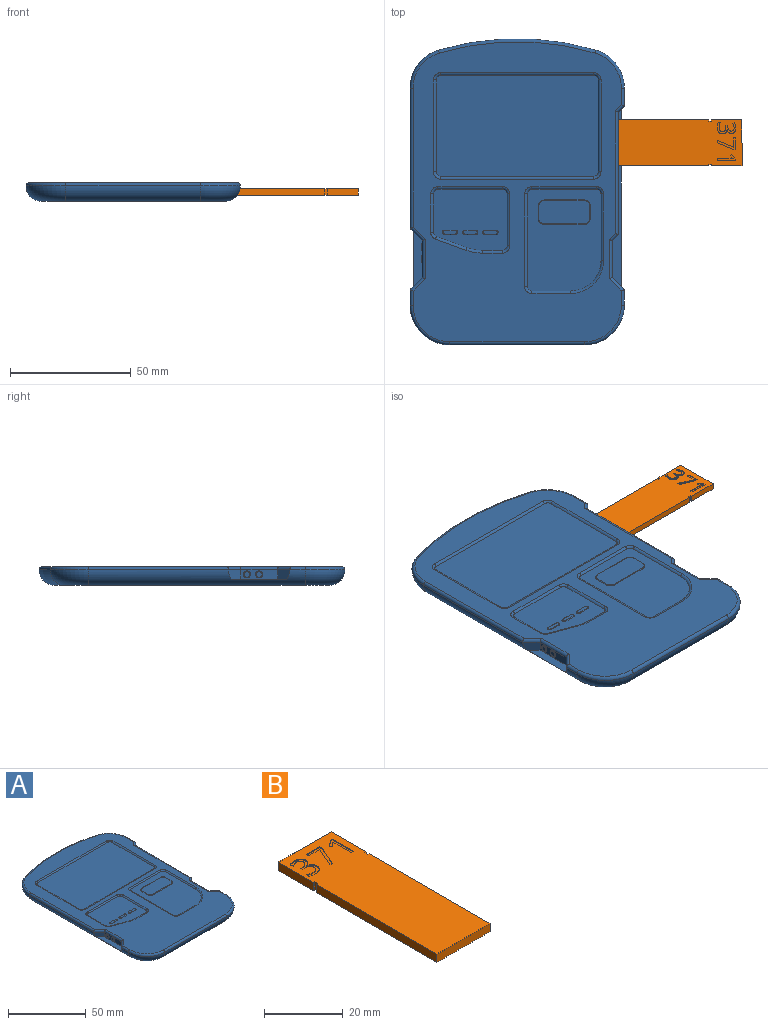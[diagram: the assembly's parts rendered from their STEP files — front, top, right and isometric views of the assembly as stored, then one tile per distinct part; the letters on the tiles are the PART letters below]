
ASSEMBLY  parts=2 mates=1
PART A: 139 faces, bbox 92.2x138.4x11.5 mm
  f0: plane 15.24x3.81mm, normal (1,0,0), area 17.9mm2, adj f1,f24,f25,f36,f129,f130,f131,f132
  f1: plane 73.66x3.81mm, normal (0,0,1), area 130mm2, adj f0,f2,f3,f23,f24,f25,f114,f116
  f2: cylinder r=6.35mm len=89.9mm, axis (0,1,0), area 580.4mm2, adj f1,f7,f11,f13,f23,f25,f31,f40
  f3: plane 50.8x3.81mm, normal (1,0,0), area 175.7mm2, adj f1,f23,f24,f32,f95,f96,f97,f98
  f4: plane 30.54x25.4mm, normal (0,0,1), area 685.8mm2, adj f49,f50,f51,f52,f53,f54,f55,f56
  f5: plane 124.46x86.36mm, normal (0,0,1), area 4712mm2, adj f15,f16,f17,f18,f19,f20,f21,f22
  f6: cylinder r=6.35mm len=89.9mm, axis (0,-1,0), area 798.1mm2, adj f7,f8,f10,f26,f27,f29,f39,f47
  f7: plane 114.3x76.2mm, normal (0,0,-1), area 8471mm2, adj f2,f6,f8,f9,f10,f11,f12,f13
  f8: torus R=10.16mm, axis (0,0,1), area 222.5mm2, adj f6,f7,f9,f46
  f9: cylinder r=6.35mm len=55.88mm, axis (1,0,0), area 557.4mm2, adj f7,f8,f11,f44
  f10: torus R=10.16mm, axis (0,0,1), area 181.5mm2, adj f6,f7,f12,f37
  f11: torus R=10.16mm, axis (0,0,1), area 222.5mm2, adj f2,f7,f9,f42
  f12: torus R=107.95mm, axis (0,0,1), area 647.3mm2, adj f7,f10,f13,f35
  f13: torus R=10.16mm, axis (0,0,1), area 181.5mm2, adj f2,f7,f12,f33
  f14: plane 67.31x41.91mm, normal (0,0,1), area 2817.8mm2, adj f15,f16,f17,f18,f19,f20,f21,f22
  f15: cylinder r=1.27mm len=63.5mm, axis (-1,0,0), area 84.5mm2, adj f5,f14,f16,f17
  f16: torus R=3mm, axis (0,0,1), area 5mm2, adj f5,f14,f15,f18
  f17: torus R=3mm, axis (0,0,1), area 5mm2, adj f5,f14,f15,f19
  f18: cylinder r=1.27mm len=38.1mm, axis (0,1,0), area 50.7mm2, adj f5,f14,f16,f20
  f19: cylinder r=1.27mm len=38.1mm, axis (0,1,0), area 50.7mm2, adj f5,f14,f17,f21
  f20: torus R=3mm, axis (0,0,1), area 5mm2, adj f5,f14,f18,f22
  f21: torus R=3mm, axis (0,0,1), area 5mm2, adj f5,f14,f19,f22
  f22: cylinder r=1.27mm len=63.5mm, axis (-1,0,0), area 84.5mm2, adj f5,f14,f20,f21
  f23: plane 3.81x2.54mm, normal (0.71,-0.71,0), area 11.5mm2, adj f1,f2,f3,f30
  f24: plane 3.81x2.54mm, normal (0.71,-0.71,0), area 13.7mm2, adj f0,f1,f3,f34
  f25: plane 5.08x5.08mm, normal (0.71,0.71,0), area 25.2mm2, adj f0,f1,f2,f38
  f26: plane 5.7x5.7mm, normal (-0.71,-0.71,0), area 25.2mm2, adj f6,f28,f29,f41
  f27: plane 5.7x5.7mm, normal (-0.71,0.71,0), area 25.2mm2, adj f6,f28,f29,f45
  f28: plane 15.24x3.81mm, normal (-1,0,0), area 44.7mm2, adj f26,f27,f29,f43,f122,f123
  f29: plane 22.86x3.81mm, normal (0,0,1), area 72.6mm2, adj f6,f26,f27,f28
  f30: cylinder r=1.27mm len=3.81mm, axis (0.71,0.71,0), area 7.2mm2, adj f5,f23,f31,f32
  f31: cylinder r=1.27mm len=7.35mm, axis (0,-1,0), area 14.1mm2, adj f2,f5,f30,f33
  f32: cylinder r=1.27mm len=51.33mm, axis (0,1,0), area 101.3mm2, adj f3,f5,f30,f34
  f33: torus R=15.24mm, axis (0,0,1), area 41mm2, adj f5,f13,f31,f35
  f34: cylinder r=1.27mm len=3.81mm, axis (0.71,0.71,0), area 7.2mm2, adj f5,f24,f32,f36
  f35: torus R=113.03mm, axis (0,0,1), area 131.6mm2, adj f5,f12,f33,f37
  f36: cylinder r=1.27mm len=16.29mm, axis (0,1,0), area 31.5mm2, adj f0,f5,f34,f38
  f37: torus R=15.24mm, axis (0,0,1), area 41mm2, adj f5,f10,f35,f39
  f38: cylinder r=1.27mm len=6.35mm, axis (-0.71,0.71,0), area 14.3mm2, adj f5,f25,f36,f40
  f39: cylinder r=1.27mm len=58.15mm, axis (0,1,0), area 115.5mm2, adj f5,f6,f37,f41
  f40: cylinder r=1.27mm len=6.35mm, axis (0,-1,0), area 12.1mm2, adj f2,f5,f38,f42
  f41: cylinder r=1.27mm len=6.35mm, axis (0.71,-0.71,0), area 14.3mm2, adj f5,f26,f39,f43
  f42: torus R=15.24mm, axis (0,0,1), area 50.3mm2, adj f5,f11,f40,f44
  f43: cylinder r=1.27mm len=16.29mm, axis (0,-1,0), area 31.5mm2, adj f5,f28,f41,f45
  f44: cylinder r=1.27mm len=55.88mm, axis (-1,0,0), area 111.5mm2, adj f5,f9,f42,f46
  f45: cylinder r=1.27mm len=6.35mm, axis (-0.71,-0.71,0), area 14.3mm2, adj f5,f27,f43,f47
  f46: torus R=15.24mm, axis (0,0,1), area 50.3mm2, adj f5,f8,f44,f47
  f47: cylinder r=1.27mm len=6.35mm, axis (0,1,0), area 12.1mm2, adj f5,f6,f45,f46
  f48: plane 42.2x30.54mm, normal (0,0,1), area 1037.6mm2, adj f59,f60,f61,f62,f63,f64,f65,f66
  f49: cylinder r=1.27mm len=8.26mm, axis (-1,0,0), area 11mm2, adj f4,f5,f50,f51
  f50: torus R=20.15mm, axis (0,0,1), area 9.1mm2, adj f4,f5,f49,f52
  f51: torus R=3mm, axis (0,0,1), area 5mm2, adj f4,f5,f49,f53
  f52: cylinder r=1.27mm len=12.99mm, axis (-0.94,0.34,0), area 17.9mm2, adj f4,f5,f50,f54
  f53: cylinder r=1.27mm len=21.59mm, axis (0,1,0), area 28.7mm2, adj f4,f5,f51,f55
  f54: torus R=3mm, axis (0,0,1), area 3.9mm2, adj f4,f5,f52,f56
  f55: torus R=3mm, axis (0,0,1), area 5mm2, adj f4,f5,f53,f57
  f56: cylinder r=1.27mm len=15.97mm, axis (0,1,0), area 21.2mm2, adj f4,f5,f54,f58
  f57: cylinder r=1.27mm len=26.73mm, axis (-1,0,0), area 35.6mm2, adj f4,f5,f55,f58
  f58: torus R=3mm, axis (0,0,1), area 5mm2, adj f4,f5,f56,f57
  f59: torus R=3mm, axis (0,0,1), area 5mm2, adj f5,f48,f60,f61
  f60: cylinder r=1.27mm len=27.6mm, axis (0,-1,0), area 36.7mm2, adj f5,f48,f59,f62
  f61: cylinder r=1.27mm len=26.73mm, axis (-1,0,0), area 35.6mm2, adj f5,f48,f59,f63
  f62: torus R=13.8mm, axis (0,0,1), area 27.6mm2, adj f5,f48,f60,f64
  f63: torus R=3mm, axis (0,0,1), area 5mm2, adj f5,f48,f61,f65
  f64: cylinder r=1.27mm len=15.94mm, axis (1,0,0), area 21.2mm2, adj f5,f48,f62,f66
  f65: cylinder r=1.27mm len=38.39mm, axis (0,1,0), area 51.1mm2, adj f5,f48,f63,f66
  f66: torus R=3mm, axis (0,0,1), area 5mm2, adj f5,f48,f64,f65
  f67: plane 5.84x1.4mm, normal (0,0,1), area 7.7mm2, adj f78,f79,f80,f81
  f68: plane 5.84x1.4mm, normal (0,0,1), area 7.7mm2, adj f74,f75,f76,f77
  f69: plane 5.84x1.4mm, normal (0,0,1), area 7.7mm2, adj f70,f71,f72,f73
  f70: cylinder r=0.25mm len=4.45mm, axis (-1,0,0), area 1.8mm2, adj f4,f69,f71,f72
  f71: torus R=0.7mm, axis (0,0,1), area 1.1mm2, adj f4,f69,f70,f73
  f72: torus R=0.7mm, axis (0,0,1), area 1.1mm2, adj f4,f69,f70,f73
  f73: cylinder r=0.25mm len=4.45mm, axis (1,0,0), area 1.8mm2, adj f4,f69,f71,f72
  f74: torus R=0.7mm, axis (0,0,1), area 1.1mm2, adj f4,f68,f75,f76
  f75: cylinder r=0.25mm len=4.45mm, axis (-1,0,0), area 1.8mm2, adj f4,f68,f74,f77
  f76: cylinder r=0.25mm len=4.45mm, axis (1,0,0), area 1.8mm2, adj f4,f68,f74,f77
  f77: torus R=0.7mm, axis (0,0,1), area 1.1mm2, adj f4,f68,f75,f76
  f78: cylinder r=0.25mm len=4.45mm, axis (1,0,0), area 1.8mm2, adj f4,f67,f79,f80
  f79: torus R=0.7mm, axis (0,0,1), area 1.1mm2, adj f4,f67,f78,f81
  f80: torus R=0.7mm, axis (0,0,1), area 1.1mm2, adj f4,f67,f78,f81
  f81: cylinder r=0.25mm len=4.45mm, axis (-1,0,0), area 1.8mm2, adj f4,f67,f79,f80
  f82: plane 21.14x9.65mm, normal (0,0,1), area 199.6mm2, adj f83,f84,f85,f86,f87,f88,f89,f90
  f83: torus R=2.29mm, axis (0,0,1), area 1.5mm2, adj f48,f82,f84,f85
  f84: cylinder r=0.25mm len=5.08mm, axis (0,-1,0), area 2mm2, adj f48,f82,f83,f86
  f85: cylinder r=0.25mm len=16.57mm, axis (-1,0,0), area 6.6mm2, adj f48,f82,f83,f87
  f86: torus R=2.29mm, axis (0,0,1), area 1.5mm2, adj f48,f82,f84,f88
  f87: torus R=2.29mm, axis (0,0,1), area 1.5mm2, adj f48,f82,f85,f89
  f88: cylinder r=0.25mm len=16.57mm, axis (1,0,0), area 6.6mm2, adj f48,f82,f86,f90
  f89: cylinder r=0.25mm len=5.08mm, axis (0,1,0), area 2mm2, adj f48,f82,f87,f90
  f90: torus R=2.29mm, axis (0,0,1), area 1.5mm2, adj f48,f82,f88,f89
  f91: plane 2.54x2.54mm, normal (1,0,0), area 2.4mm2, adj f107,f108,f109,f110
  f92: plane 2.54x2.54mm, normal (1,0,0), area 2.4mm2, adj f103,f104,f105,f106
  f93: plane 2.54x2.54mm, normal (1,0,0), area 2.4mm2, adj f99,f100,f101,f102
  f94: plane 2.54x2.54mm, normal (1,0,0), area 2.4mm2, adj f95,f96,f97,f98
  f95: torus R=0.38mm, axis (1,0,0), area 0.7mm2, adj f3,f94,f96,f97
  f96: cylinder r=0.25mm len=1.96mm, axis (0,-0.71,0.71), area 1mm2, adj f3,f94,f95,f98
  f97: cylinder r=0.25mm len=1.96mm, axis (0,0.71,-0.71), area 1mm2, adj f3,f94,f95,f98
  f98: torus R=0.38mm, axis (1,0,0), area 0.7mm2, adj f3,f94,f96,f97
  f99: torus R=0.38mm, axis (1,0,0), area 0.7mm2, adj f3,f93,f100,f101
  f100: cylinder r=0.25mm len=1.96mm, axis (0,-0.71,0.71), area 1mm2, adj f3,f93,f99,f102
  f101: cylinder r=0.25mm len=1.96mm, axis (0,0.71,-0.71), area 1mm2, adj f3,f93,f99,f102
  f102: torus R=0.38mm, axis (1,0,0), area 0.7mm2, adj f3,f93,f100,f101
  f103: cylinder r=0.25mm len=1.96mm, axis (0,0.71,-0.71), area 1mm2, adj f3,f92,f104,f105
  f104: torus R=0.38mm, axis (1,0,0), area 0.7mm2, adj f3,f92,f103,f106
  f105: torus R=0.38mm, axis (1,0,0), area 0.7mm2, adj f3,f92,f103,f106
  f106: cylinder r=0.25mm len=1.96mm, axis (0,-0.71,0.71), area 1mm2, adj f3,f92,f104,f105
  f107: cylinder r=0.25mm len=1.96mm, axis (0,0.71,-0.71), area 1mm2, adj f3,f91,f108,f109
  f108: torus R=0.38mm, axis (1,0,0), area 0.7mm2, adj f3,f91,f107,f110
  f109: torus R=0.38mm, axis (1,0,0), area 0.7mm2, adj f3,f91,f107,f110
  f110: cylinder r=0.25mm len=1.96mm, axis (0,-0.71,0.71), area 1mm2, adj f3,f91,f108,f109
  f111: plane 3.99x0.48mm, normal (1,0,0), area 1.9mm2, adj f112,f113,f116,f117
  f112: cylinder r=2.54mm len=1.42mm, axis (0,0,-1), area 0.4mm2, adj f111,f114,f115
  f113: cylinder r=2.54mm len=1.42mm, axis (0,0,-1), area 0.4mm2, adj f111,f118,f119
  f114: torus R=2.79mm, axis (0,0,1), area 0.8mm2, adj f1,f2,f112,f115,f116
  f115: bspline ~2.69x1.45mm, area 0.4mm2, adj f2,f112,f114,f117
  f116: cylinder r=0.25mm len=3.99mm, axis (0,1,0), area 1.6mm2, adj f1,f111,f114,f118
  f117: cylinder r=0.25mm len=3.99mm, axis (0,1,0), area 0.9mm2, adj f2,f111,f115,f119
  f118: torus R=2.79mm, axis (0,0,1), area 0.8mm2, adj f1,f2,f113,f116,f119
  f119: bspline ~2.69x1.45mm, area 0.4mm2, adj f2,f113,f117,f118
  f120: plane 2.41x2.41mm, normal (-1,0,0), area 4.6mm2, adj f123
  f121: plane 2.41x2.41mm, normal (-1,0,0), area 4.6mm2, adj f122
  f122: torus R=1.21mm, axis (-1,0,0), area 3.4mm2, adj f28,f121
  f123: torus R=1.21mm, axis (-1,0,0), area 3.4mm2, adj f28,f120
  f124: cylinder r=1.14mm len=2.29mm, axis (1,0,0), area 0.9mm2, adj f125,f127,f128,f129
  f125: plane 12.19x0.25mm, normal (0,0,-1), area 3.1mm2, adj f124,f126,f128,f130
  f126: cylinder r=1.14mm len=2.29mm, axis (1,0,0), area 0.9mm2, adj f125,f127,f128,f132
  f127: plane 12.19x0.25mm, normal (0,0,1), area 3.1mm2, adj f124,f126,f128,f131
  f128: plane 14.48x2.29mm, normal (1,0,0), area 32mm2, adj f124,f125,f126,f127
  f129: torus R=1.4mm, axis (-1,0,0), area 1.5mm2, adj f0,f124,f130,f131
  f130: cylinder r=0.25mm len=12.19mm, axis (0,-1,0), area 4.9mm2, adj f0,f125,f129,f132
  f131: cylinder r=0.25mm len=12.19mm, axis (0,1,0), area 4.9mm2, adj f0,f127,f129,f132
  f132: torus R=1.4mm, axis (-1,0,0), area 1.5mm2, adj f0,f126,f130,f131
  f133: plane 19.05x2.54mm, normal (-1,0,0), area 48.4mm2, adj f135,f136,f137,f138
  f134: plane 19.05x2.54mm, normal (1,0,0), area 48.4mm2, adj f135,f136,f137,f138
  f135: plane 4.06x2.54mm, normal (0,-1,0), area 10.3mm2, adj f133,f134,f137,f138
  f136: plane 4.06x2.54mm, normal (0,1,0), area 10.3mm2, adj f133,f134,f137,f138
  f137: plane 19.05x4.06mm, normal (0,0,-1), area 77.4mm2, adj f133,f134,f135,f136
  f138: plane 19.05x4.06mm, normal (0,0,1), area 77.4mm2, adj f133,f134,f135,f136
PART B: 56 faces, bbox 19.1x57.2x2.5 mm
  f0: plane 57.15x19.05mm, normal (0,0,1), area 1055mm2, adj f1,f2,f3,f4,f5,f6,f7,f8
  f1: plane 2.54x0.51mm, normal (0,1,0), area 1.3mm2, adj f0,f2,f12,f13
  f2: plane 43.43x2.54mm, normal (-1,0,0), area 110.3mm2, adj f0,f1,f3,f13
  f3: plane 19.05x2.54mm, normal (0,-1,0), area 48.4mm2, adj f0,f2,f4,f13
  f4: plane 43.43x2.54mm, normal (1,0,0), area 110.3mm2, adj f0,f3,f5,f13
  f5: plane 2.54x0.51mm, normal (0,1,0), area 1.3mm2, adj f0,f4,f6,f13
  f6: plane 2.54x1.02mm, normal (1,0,0), area 2.6mm2, adj f0,f5,f7,f13
  f7: plane 2.54x0.51mm, normal (0,-1,0), area 1.3mm2, adj f0,f6,f8,f13
  f8: plane 12.7x2.54mm, normal (1,0,0), area 32.3mm2, adj f0,f7,f9,f13
  f9: plane 19.05x2.54mm, normal (0,1,0), area 48.4mm2, adj f0,f8,f10,f13
  f10: plane 12.7x2.54mm, normal (-1,0,0), area 32.3mm2, adj f0,f9,f11,f13
  f11: plane 2.54x0.51mm, normal (0,-1,0), area 1.3mm2, adj f0,f10,f12,f13
  f12: plane 2.54x1.02mm, normal (-1,0,0), area 2.6mm2, adj f0,f1,f11,f13
  f13: plane 57.15x19.05mm, normal (0,0,-1), area 1087.7mm2, adj f1,f2,f3,f4,f5,f6,f7,f8
  f14: plane 0.91x0.25mm, normal (0,1,0), area 0.2mm2, adj f0,f15,f22,f23
  f15: plane 7.56x0.25mm, normal (-1,0,0), area 1.9mm2, adj f0,f14,f16,f23
  f16: plane 0.78x0.25mm, normal (0,-1,0), area 0.2mm2, adj f0,f15,f17,f23
  f17: plane 1.98x1.55mm, normal (0.62,-0.79,0), area 0.6mm2, adj f0,f16,f18,f23
  f18: plane 0.64x0.5mm, normal (0.79,0.62,0), area 0.2mm2, adj f0,f17,f19,f23
  f19: plane 0.76x0.63mm, normal (-0.63,0.77,0), area 0.3mm2, adj f0,f18,f20,f23
  f20: extruded ~0.63x0.58mm, area 0.2mm2, adj f0,f19,f21,f23
  f21: extruded ~1.87x0.25mm, area 0.5mm2, adj f0,f20,f22,f23
  f22: plane 4.72x0.25mm, normal (1,0,0), area 1.2mm2, adj f0,f14,f21,f23
  f23: plane 7.56x2.76mm, normal (0,0,1), area 8.4mm2, adj f14,f15,f16,f17,f18,f19,f20,f21
  f24: plane 6.7x2.91mm, normal (0.92,-0.4,0), area 1.9mm2, adj f0,f25,f30,f31
  f25: plane 1x0.25mm, normal (0,1,0), area 0.3mm2, adj f0,f24,f26,f31
  f26: plane 6.81x2.87mm, normal (-0.92,0.39,0), area 1.9mm2, adj f0,f25,f27,f31
  f27: plane 0.75x0.25mm, normal (-1,0,0), area 0.2mm2, adj f0,f26,f28,f31
  f28: plane 4.86x0.25mm, normal (0,-1,0), area 1.2mm2, adj f0,f27,f29,f31
  f29: plane 0.86x0.25mm, normal (1,0,0), area 0.2mm2, adj f0,f28,f30,f31
  f30: plane 3.9x0.25mm, normal (0,1,0), area 1mm2, adj f0,f24,f29,f31
  f31: plane 7.56x4.86mm, normal (0,0,1), area 10.6mm2, adj f24,f25,f26,f27,f28,f29,f30
  f32: plane 0.25x0.03mm, normal (-1,0,0), area 0mm2, adj f0,f33,f54,f55
  f33: extruded ~1.21x0.62mm, area 0.4mm2, adj f0,f32,f34,f55
  f34: extruded ~1.19x0.42mm, area 0.3mm2, adj f0,f33,f35,f55
  f35: extruded ~1.36x0.6mm, area 0.4mm2, adj f0,f34,f36,f55
  f36: extruded ~1.66x0.51mm, area 0.5mm2, adj f0,f35,f37,f55
  f37: extruded ~2.25x0.77mm, area 0.6mm2, adj f0,f36,f38,f55
  f38: plane 0.65x0.48mm, normal (0.81,0.59,0), area 0.2mm2, adj f0,f37,f39,f55
  f39: extruded ~1.78x0.63mm, area 0.5mm2, adj f0,f38,f40,f55
  f40: extruded ~0.94x0.31mm, area 0.3mm2, adj f0,f39,f41,f55
  f41: extruded ~0.83x0.35mm, area 0.2mm2, adj f0,f40,f42,f55
  f42: extruded ~1.04x0.45mm, area 0.3mm2, adj f0,f41,f43,f55
  f43: extruded ~1.28x0.39mm, area 0.3mm2, adj f0,f42,f44,f55
  f44: plane 0.69x0.25mm, normal (0,-1,0), area 0.2mm2, adj f0,f43,f45,f55
  f45: plane 0.78x0.25mm, normal (1,0,0), area 0.2mm2, adj f0,f44,f46,f55
  f46: plane 0.69x0.25mm, normal (0,1,0), area 0.2mm2, adj f0,f45,f47,f55
  f47: extruded ~1.97x1.33mm, area 0.7mm2, adj f0,f46,f48,f55
  f48: extruded ~1.83x1.49mm, area 0.7mm2, adj f0,f47,f49,f55
  f49: extruded ~1.98x0.5mm, area 0.5mm2, adj f0,f48,f50,f55
  f50: plane 0.88x0.25mm, normal (1,0,0), area 0.2mm2, adj f0,f49,f51,f55
  f51: extruded ~2x0.41mm, area 0.5mm2, adj f0,f50,f52,f55
  f52: extruded ~2.06x0.6mm, area 0.6mm2, adj f0,f51,f53,f55
  f53: extruded ~1.65x0.71mm, area 0.5mm2, adj f0,f52,f54,f55
  f54: extruded ~1.87x1.8mm, area 0.7mm2, adj f0,f32,f53,f55
  f55: plane 7.77x4.78mm, normal (0,0,1), area 13.7mm2, adj f32,f33,f34,f35,f36,f37,f38,f39
PLACE A rot(axis=(1,0,0),0deg) t=(14.87,106.95,-11.73)mm fixed
PLACE B rot(axis=(0,0,-1),90deg) t=(50.94,187.6,-9.19)mm
MATE slider B.f3 <-> A.f134  axis (-1,0,0) through (50.94,178.07,-7.92)mm
